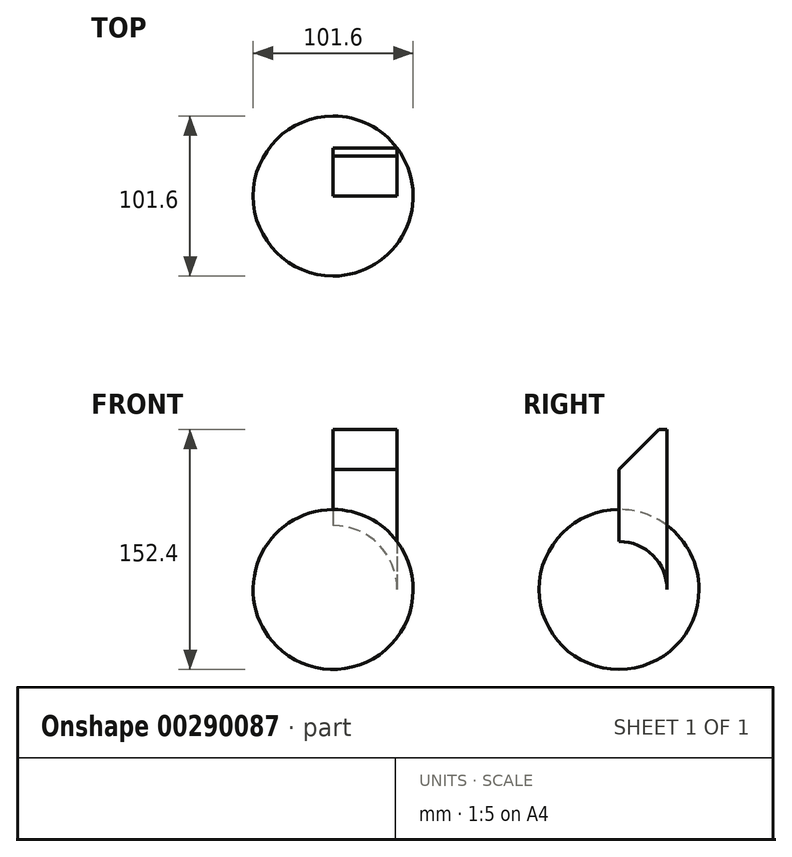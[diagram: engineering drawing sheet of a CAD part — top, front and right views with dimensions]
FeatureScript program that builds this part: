
annotation { "Feature Type Name" : "Feature", "Feature Type Description" : "" }
export const myFeature = defineFeature(function(context is Context, id is Id, definition is map)
    precondition{}
    {
        {
            var Q0;
            Q0=qCreatedBy(makeId("Top.planeOp"),FACE);
            var sketch = newSketch(context, id + "F0", { "sketchPlane" : qUnion([Q0])});
            skArc(sketch, "E0", {"start": v(0, 50.8) * mm, "mid": v(-50.8, 0) * mm, "end": v(0, -50.8) * mm});
            skLineSegment(sketch, "E1", {"start": v(0, 50.8) * mm, "end": v(0, -50.8) * mm});
            skSolve(sketch);
        }
        {
            var Q0;
            Q0 = qSketchRegion(id + "F0", true);
            var Q1;
            Q1=sQuery(id+"F0.wireOp",EDGE,"E1");
            revolve(context, id + "F1", {"entities" : qUnion([Q0]), "axis" : qUnion([Q1]), "revolveType" : RevolveType.FULL, "oppositeDirection" : true});
        }
        {
            var Q0;
            Q0=qCreatedBy(makeId("Top.planeOp"),FACE);
            var sketch = newSketch(context, id + "F2", { "sketchPlane" : qUnion([Q0])});
            skLineSegment(sketch, "E2.bottom", {"start": v(0, 0) * mm, "end": v(40.64, 0) * mm});
            skLineSegment(sketch, "E2.top", {"start": v(0, 30.48) * mm, "end": v(40.64, 30.48) * mm});
            skLineSegment(sketch, "E2.left", {"start": v(0, 0) * mm, "end": v(0, 30.48) * mm});
            skLineSegment(sketch, "E2.right", {"start": v(40.64, 0) * mm, "end": v(40.64, 30.48) * mm});
            skSolve(sketch);
        }
        {
            var Q0;
            Q0 = qSketchRegion(id + "F2", true);
            extrude(context, id + "F3", {"entities" : qUnion([Q0]), "operationType" : NewBodyOperationType.ADD, "depth" : 101.6 * mm});
        }
        {
            var Q0;
            Q0=makeQuery(id+"F3.opExtrude","CAP_EDGE",EDGE,{"disambiguationData":[OSD([sQuery(id+"F2.wireOp",EDGE,"E2.bottom")])],"isStart":false});
            chamfer(context, id + "F4", {"entities" : qUnion([Q0]), "width" : 25.4 * mm, "tangentPropagation" : true});
        }
    });
